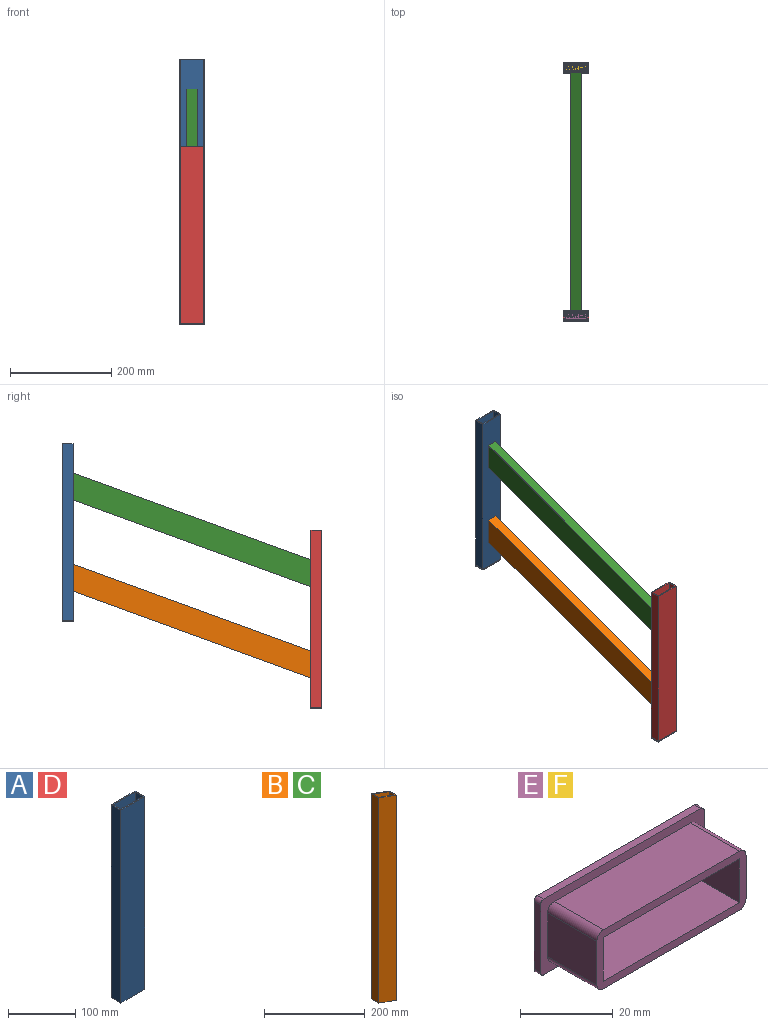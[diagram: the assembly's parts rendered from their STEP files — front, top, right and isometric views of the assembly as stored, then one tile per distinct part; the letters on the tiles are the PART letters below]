
ASSEMBLY  parts=6 mates=5
PART A: 10 faces, bbox 50x20x350 mm
  f0: plane 350x50mm, normal (0,1,0), area 17500mm2, adj f1,f7,f8,f9
  f1: plane 350x20mm, normal (-1,0,0), area 7000mm2, adj f0,f2,f8,f9
  f2: plane 350x50mm, normal (0,-1,0), area 17500mm2, adj f1,f7,f8,f9
  f3: plane 350x16mm, normal (1,0,0), area 5600mm2, adj f4,f6,f8,f9
  f4: plane 350x46mm, normal (0,-1,0), area 16100mm2, adj f3,f5,f8,f9
  f5: plane 350x16mm, normal (-1,0,0), area 5600mm2, adj f4,f6,f8,f9
  f6: plane 350x46mm, normal (0,1,0), area 16100mm2, adj f3,f5,f8,f9
  f7: plane 350x20mm, normal (1,0,0), area 7000mm2, adj f0,f2,f8,f9
  f8: plane 50x20mm, normal (0,0,1), area 264mm2, adj f0,f1,f2,f3,f4,f5,f6,f7
  f9: plane 50x20mm, normal (0,0,-1), area 264mm2, adj f0,f1,f2,f3,f4,f5,f6,f7
PART B: 10 faces, bbox 50x20x518 mm
  f0: plane 516.54x46mm, normal (0,1,0), area 22990.9mm2, adj f1,f3,f4,f5
  f1: plane 499.8x16mm, normal (-1,0,0), area 7996.8mm2, adj f0,f2,f4,f5
  f2: plane 516.54x46mm, normal (0,-1,0), area 22990.9mm2, adj f1,f3,f4,f5
  f3: plane 499.8x16mm, normal (1,0,0), area 7996.8mm2, adj f0,f2,f4,f5
  f4: plane 50x20mm, normal (0.34,0,0.94), area 280.9mm2, adj f0,f1,f2,f3,f6,f7,f8,f9
  f5: plane 50x20mm, normal (-0.34,0,-0.94), area 280.9mm2, adj f0,f1,f2,f3,f6,f7,f8,f9
  f6: plane 518x50mm, normal (0,-1,0), area 24990.1mm2, adj f4,f5,f7,f9
  f7: plane 499.8x20mm, normal (1,0,0), area 9996mm2, adj f4,f5,f6,f8
  f8: plane 518x50mm, normal (0,1,0), area 24990.1mm2, adj f4,f5,f7,f9
  f9: plane 499.8x20mm, normal (-1,0,0), area 9996mm2, adj f4,f5,f6,f8
PART C: same geometry as B
PART D: same geometry as A
PART E: 121 faces, bbox 50x17x20 mm
  f0: plane 50x20mm, normal (0,1,0), area 873.8mm2, adj f2,f3,f4,f5,f20,f21,f22,f23
  f1: plane 50x20mm, normal (0,-1,0), area 291.2mm2, adj f2,f3,f4,f5,f6,f7,f8,f13
  f2: plane 48x2mm, normal (0,0,1), area 96mm2, adj f0,f1,f20,f23
  f3: plane 18x2mm, normal (-1,0,0), area 36mm2, adj f0,f1,f20,f21
  f4: plane 48x2mm, normal (0,0,-1), area 96mm2, adj f0,f1,f21,f22
  f5: plane 18x2mm, normal (1,0,0), area 36mm2, adj f0,f1,f22,f23
  f6: plane 41.6x15mm, normal (0,0,1), area 624mm2, adj f1,f14,f16,f19
  f7: plane 15x11.6mm, normal (-1,0,0), area 174mm2, adj f1,f14,f16,f17
  f8: plane 41.6x15mm, normal (0,0,-1), area 624mm2, adj f1,f14,f17,f18
  f9: plane 15x11.6mm, normal (1,0,0), area 174mm2, adj f10,f12,f14,f15
  f10: plane 41.6x15mm, normal (0,0,-1), area 624mm2, adj f9,f11,f14,f15
  f11: plane 15x11.6mm, normal (-1,0,0), area 174mm2, adj f10,f12,f14,f15
  f12: plane 41.6x15mm, normal (0,0,1), area 624mm2, adj f9,f11,f14,f15
  f13: plane 15x11.6mm, normal (1,0,0), area 174mm2, adj f1,f14,f18,f19
  f14: plane 45.6x15.6mm, normal (0,-1,0), area 225.4mm2, adj f6,f7,f8,f9,f10,f11,f12,f13
  f15: plane 41.6x11.6mm, normal (0,-1,0), area 482.6mm2, adj f9,f10,f11,f12
  f16: cylinder r=2mm len=15mm, axis (0,-1,0), area 47.1mm2, adj f1,f6,f7,f14
  f17: cylinder r=2mm len=15mm, axis (0,1,0), area 47.1mm2, adj f1,f7,f8,f14
  f18: cylinder r=2mm len=15mm, axis (0,-1,0), area 47.1mm2, adj f1,f8,f13,f14
  f19: cylinder r=2mm len=15mm, axis (0,1,0), area 47.1mm2, adj f1,f6,f13,f14
  f20: cylinder r=1mm len=2mm, axis (0,-1,0), area 3.1mm2, adj f0,f1,f2,f3
  f21: cylinder r=1mm len=2mm, axis (0,1,0), area 3.1mm2, adj f0,f1,f3,f4
  f22: cylinder r=1mm len=2mm, axis (0,-1,0), area 3.1mm2, adj f0,f1,f4,f5
  f23: cylinder r=1mm len=2mm, axis (0,1,0), area 3.1mm2, adj f0,f1,f2,f5
  f24: plane 1.3x1mm, normal (0,0,-1), area 1.3mm2, adj f0,f25,f33,f34
  f25: plane 3.61x1.15mm, normal (-0.95,0,-0.3), area 3.8mm2, adj f0,f24,f26,f34
  f26: extruded ~1.33x1mm, area 1.4mm2, adj f0,f25,f27,f34
  f27: extruded ~1x0.59mm, area 0.6mm2, adj f0,f26,f28,f34
  f28: extruded ~1x0.74mm, area 0.8mm2, adj f0,f27,f29,f34
  f29: plane 3.61x1.14mm, normal (0.95,0,-0.3), area 3.8mm2, adj f0,f28,f30,f34
  f30: plane 1.3x1mm, normal (0,0,-1), area 1.3mm2, adj f0,f29,f31,f34
  f31: plane 6.06x2.06mm, normal (-0.95,0,0.32), area 6.4mm2, adj f0,f30,f32,f34
  f32: plane 1.4x1mm, normal (0,0,1), area 1.4mm2, adj f0,f31,f33,f34
  f33: plane 6.06x2.06mm, normal (0.95,0,0.32), area 6.4mm2, adj f0,f24,f32,f34
  f34: plane 6.06x5.52mm, normal (0,1,0), area 14.2mm2, adj f24,f25,f26,f27,f28,f29,f30,f31
  f35: plane 1.63x1mm, normal (0,0,1), area 1.6mm2, adj f0,f36,f48,f49
  f36: plane 6.06x1mm, normal (1,0,0), area 6.1mm2, adj f0,f35,f37,f49
  f37: plane 1.16x1mm, normal (0,0,-1), area 1.2mm2, adj f0,f36,f38,f49
  f38: plane 2.87x1mm, normal (-1,0,0), area 2.9mm2, adj f0,f37,f39,f49
  f39: extruded ~1.67x1mm, area 1.7mm2, adj f0,f38,f40,f49
  f40: plane 1x0.03mm, normal (0,0,-1), area 0mm2, adj f0,f39,f41,f49
  f41: plane 4.54x2.63mm, normal (0.87,0,-0.5), area 5.2mm2, adj f0,f40,f42,f49
  f42: plane 1.62x1mm, normal (0,0,-1), area 1.6mm2, adj f0,f41,f43,f49
  f43: plane 6.06x1mm, normal (-1,0,0), area 6.1mm2, adj f0,f42,f44,f49
  f44: plane 1.15x1mm, normal (0,0,1), area 1.1mm2, adj f0,f43,f45,f49
  f45: plane 2.85x1mm, normal (1,0,0), area 2.9mm2, adj f0,f44,f46,f49
  f46: extruded ~1.73x1mm, area 1.7mm2, adj f0,f45,f47,f49
  f47: plane 1x0.04mm, normal (0,0,1), area 0mm2, adj f0,f46,f48,f49
  f48: plane 4.58x2.64mm, normal (-0.87,0,0.5), area 5.3mm2, adj f0,f35,f47,f49
  f49: plane 6.06x5.38mm, normal (0,1,0), area 20.8mm2, adj f35,f36,f37,f38,f39,f40,f41,f42
  f50: extruded ~2.22x1mm, area 2.3mm2, adj f51,f61,f62,f120
  f51: plane 1.58x1mm, normal (0,0,-1), area 1.6mm2, adj f50,f52,f62,f120
  f52: extruded ~2.62x1mm, area 2.7mm2, adj f51,f61,f62,f120
  f53: plane 1.44x1mm, normal (-0.96,0,0.29), area 1.5mm2, adj f0,f54,f60,f62
  f54: plane 1.38x1mm, normal (0,0,1), area 1.4mm2, adj f0,f53,f55,f62
  f55: plane 6.08x2.15mm, normal (0.94,0,-0.33), area 6.5mm2, adj f0,f54,f56,f62
  f56: plane 1.57x1mm, normal (0,0,-1), area 1.6mm2, adj f0,f55,f57,f62
  f57: plane 6.08x2.14mm, normal (-0.94,0,-0.33), area 6.4mm2, adj f0,f56,f58,f62
  f58: plane 1.38x1mm, normal (0,0,1), area 1.4mm2, adj f0,f57,f59,f62
  f59: plane 1.44x1mm, normal (0.96,0,0.29), area 1.5mm2, adj f0,f58,f60,f62
  f60: plane 2.21x1mm, normal (0,0,1), area 2.2mm2, adj f0,f53,f59,f62
  f61: extruded ~1x0.41mm, area 0.4mm2, adj f50,f52,f62,f120
  f62: plane 6.08x5.86mm, normal (0,1,0), area 16.7mm2, adj f50,f51,f52,f53,f54,f55,f56,f57
  f63: plane 6.06x1mm, normal (-1,0,0), area 6.1mm2, adj f0,f64,f66,f67
  f64: plane 1.29x1mm, normal (0,0,1), area 1.3mm2, adj f0,f63,f65,f67
  f65: plane 6.06x1mm, normal (1,0,0), area 6.1mm2, adj f0,f64,f66,f67
  f66: plane 1.29x1mm, normal (0,0,-1), area 1.3mm2, adj f0,f63,f65,f67
  f67: plane 6.06x1.29mm, normal (0,1,0), area 7.8mm2, adj f63,f64,f65,f66
  f68: plane 1.29x1mm, normal (0,0,1), area 1.3mm2, adj f0,f69,f75,f76
  f69: plane 4.99x1mm, normal (1,0,0), area 5mm2, adj f0,f68,f70,f76
  f70: plane 1.64x1mm, normal (0,0,1), area 1.6mm2, adj f0,f69,f71,f76
  f71: plane 1.07x1mm, normal (1,0,0), area 1.1mm2, adj f0,f70,f72,f76
  f72: plane 4.58x1mm, normal (0,0,-1), area 4.6mm2, adj f0,f71,f73,f76
  f73: plane 1.07x1mm, normal (-1,0,0), area 1.1mm2, adj f0,f72,f74,f76
  f74: plane 1.65x1mm, normal (0,0,1), area 1.6mm2, adj f0,f73,f75,f76
  f75: plane 4.99x1mm, normal (-1,0,0), area 5mm2, adj f0,f68,f74,f76
  f76: plane 6.06x4.58mm, normal (0,1,0), area 11.3mm2, adj f68,f69,f70,f71,f72,f73,f74,f75
  f77: plane 6.06x1mm, normal (-1,0,0), area 6.1mm2, adj f0,f78,f82,f83
  f78: plane 3.74x1mm, normal (0,0,1), area 3.7mm2, adj f0,f77,f79,f83
  f79: plane 1.06x1mm, normal (1,0,0), area 1.1mm2, adj f0,f78,f80,f83
  f80: plane 2.46x1mm, normal (0,0,-1), area 2.5mm2, adj f0,f79,f81,f83
  f81: plane 5x1mm, normal (1,0,0), area 5mm2, adj f0,f80,f82,f83
  f82: plane 1.29x1mm, normal (0,0,-1), area 1.3mm2, adj f0,f77,f81,f83
  f83: plane 6.06x3.74mm, normal (0,1,0), area 10.4mm2, adj f77,f78,f79,f80,f81,f82
  f84: plane 3.92x1mm, normal (1,0,0), area 3.9mm2, adj f0,f85,f98,f99
  f85: plane 1.28x1mm, normal (0,0,-1), area 1.3mm2, adj f0,f84,f86,f99
  f86: plane 3.7x1mm, normal (-1,0,0), area 3.7mm2, adj f0,f85,f87,f99
  f87: extruded ~1.03x1mm, area 1.1mm2, adj f0,f86,f88,f99
  f88: extruded ~1x0.91mm, area 1mm2, adj f0,f87,f89,f99
  f89: extruded ~1x0.93mm, area 1mm2, adj f0,f88,f90,f99
  f90: extruded ~1.03x1mm, area 1.1mm2, adj f0,f89,f91,f99
  f91: plane 3.71x1mm, normal (1,0,0), area 3.7mm2, adj f0,f90,f92,f99
  f92: plane 1.28x1mm, normal (0,0,-1), area 1.3mm2, adj f0,f91,f93,f99
  f93: plane 3.9x1mm, normal (-1,0,0), area 3.9mm2, adj f0,f92,f94,f99
  f94: extruded ~1.64x1mm, area 1.8mm2, adj f0,f93,f95,f99
  f95: extruded ~1.82x1mm, area 2mm2, adj f0,f94,f96,f99
  f96: extruded ~1.34x1mm, area 1.4mm2, adj f0,f95,f97,f99
  f97: extruded ~1x0.87mm, area 1.2mm2, adj f0,f96,f98,f99
  f98: extruded ~1.18x1mm, area 1.2mm2, adj f0,f84,f97,f99
  f99: plane 6.14x4.97mm, normal (0,1,0), area 16.8mm2, adj f84,f85,f86,f87,f88,f89,f90,f91
  f100: plane 4.75x1.46mm, normal (-0.96,0,0.29), area 5mm2, adj f0,f101,f118,f119
  f101: plane 1.18x1mm, normal (0,0,1), area 1.2mm2, adj f0,f100,f102,f119
  f102: plane 4.75x1.56mm, normal (0.95,0,0.31), area 5mm2, adj f0,f101,f103,f119
  f103: plane 1x0.04mm, normal (0,0,1), area 0mm2, adj f0,f102,f104,f119
  f104: extruded ~1.41x1mm, area 1.4mm2, adj f0,f103,f105,f119
  f105: extruded ~1x0.47mm, area 0.5mm2, adj f0,f104,f106,f119
  f106: plane 2.87x1mm, normal (-1,0,0), area 2.9mm2, adj f0,f105,f107,f119
  f107: plane 1.2x1mm, normal (0,0,1), area 1.2mm2, adj f0,f106,f108,f119
  f108: plane 6.06x1mm, normal (1,0,0), area 6.1mm2, adj f0,f107,f109,f119
  f109: plane 1.75x1mm, normal (0,0,-1), area 1.7mm2, adj f0,f108,f110,f119
  f110: plane 4.63x1.52mm, normal (-0.95,0,-0.31), area 4.9mm2, adj f0,f109,f111,f119
  f111: plane 1x0.03mm, normal (0,0,-1), area 0mm2, adj f0,f110,f112,f119
  f112: plane 4.63x1.43mm, normal (0.96,0,-0.3), area 4.9mm2, adj f0,f111,f113,f119
  f113: plane 1.75x1mm, normal (0,0,-1), area 1.7mm2, adj f0,f112,f114,f119
  f114: plane 6.06x1mm, normal (-1,0,0), area 6.1mm2, adj f0,f113,f115,f119
  f115: plane 1.15x1mm, normal (0,0,1), area 1.1mm2, adj f0,f114,f116,f119
  f116: plane 2.82x1mm, normal (1,0,0), area 2.8mm2, adj f0,f115,f117,f119
  f117: extruded ~1.94x1mm, area 1.9mm2, adj f0,f116,f118,f119
  f118: plane 1x0.04mm, normal (0,0,1), area 0mm2, adj f0,f100,f117,f119
  f119: plane 6.48x6.06mm, normal (0,1,0), area 25.3mm2, adj f100,f101,f102,f103,f104,f105,f106,f107
  f120: plane 2.62x1.58mm, normal (0,1,0), area 2mm2, adj f50,f51,f52,f61
PART F: same geometry as E
PLACE A t=(-153.08,493.49,170.58)mm
PLACE B rot(axis=(-0.5,0.5,0.71),109.2deg) t=(-153.08,5.28,81.52)mm
PLACE C rot(axis=(-0.5,0.5,0.71),109.2deg) t=(-153.08,5.28,261.52)mm
PLACE D t=(-153.08,3.83,-0.37)mm
PLACE E rot(axis=(-1,0,0),90deg) t=(-153.08,3.83,-2.37)mm
PLACE F rot(axis=(-1,0,0),90deg) t=(-153.08,493.49,168.58)mm
MATE fastened C.f5 <-> D.f0  axis (0,-1,0) through (-153.08,13.83,264.63)mm
MATE fastened A.f2 <-> B.f4  axis (0,-1,0) through (-153.08,483.49,345.58)mm
MATE fastened E.f15 <-> D.f9  axis (0,0,1) through (-153.08,3.83,-0.37)mm
MATE fastened B.f5 <-> D.f0  axis (0,-1,0) through (-153.08,13.83,84.63)mm
MATE fastened F.f15 <-> A.f9  axis (0,0,1) through (-153.08,493.49,170.58)mm
